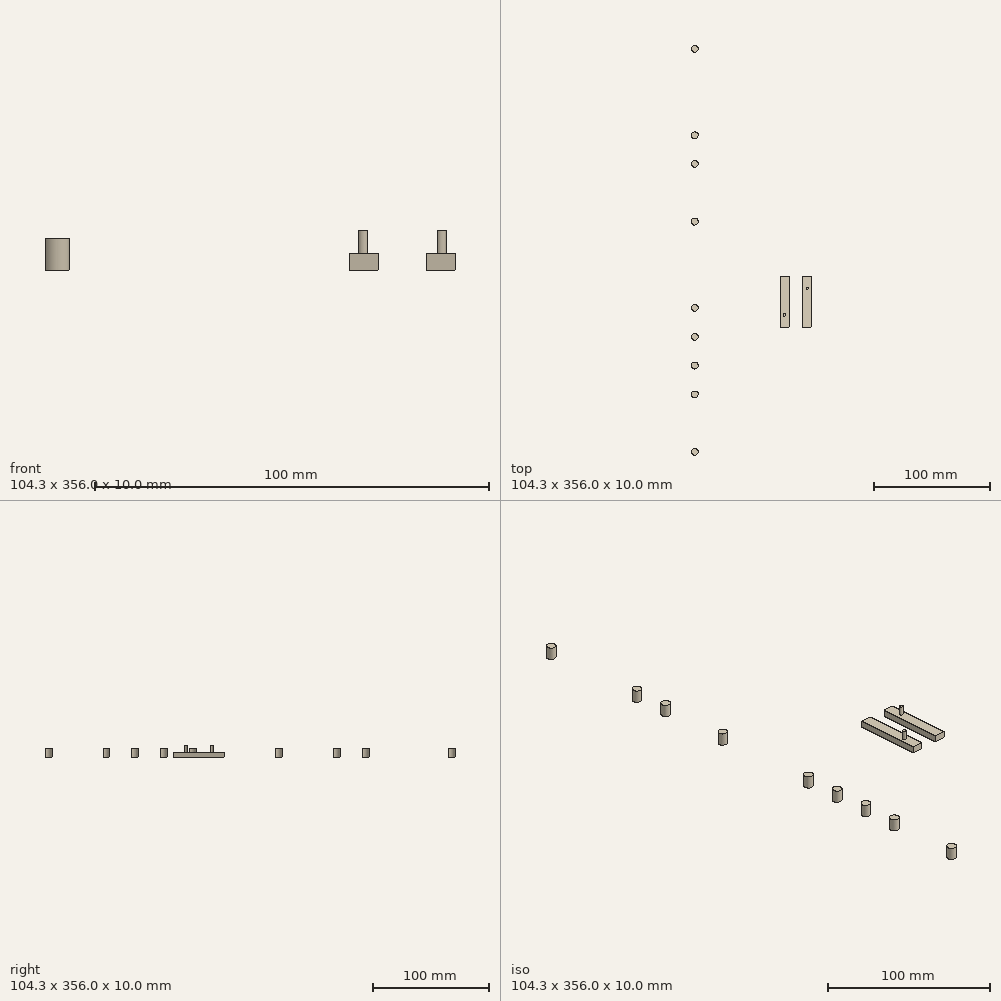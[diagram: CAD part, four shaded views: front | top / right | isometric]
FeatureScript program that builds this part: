
annotation { "Feature Type Name" : "Feature", "Feature Type Description" : "" }
export const myFeature = defineFeature(function(context is Context, id is Id, definition is map)
    precondition{}
    {
        {
            var Q0;
            Q0=qCreatedBy(makeId("Top.planeOp"),FACE);
            var sketch = newSketch(context, id + "F0", { "sketchPlane" : qUnion([Q0])});
            skLineSegment(sketch, "E0.bottom", {"start": v(-46.21, 327.74) * mm, "end": v(-34.21, 327.74) * mm});
            skLineSegment(sketch, "E0.top", {"start": v(-46.21, -72.26) * mm, "end": v(-34.21, -72.26) * mm});
            skLineSegment(sketch, "E0.left", {"start": v(-46.21, 327.74) * mm, "end": v(-46.21, -72.26) * mm});
            skLineSegment(sketch, "E0.right", {"start": v(-34.21, 327.74) * mm, "end": v(-34.21, -72.26) * mm});
            skSolve(sketch);
        }
        {
            var Q0;
            Q0=makeQuery(id+"F0.imprint","IMPRINT",FACE,{"disambiguationData":[TD([[makeQuery(id+"F0.imprint","IMPRINT",EDGE,{"derivedFrom":sQuery(id+"F0.wireOp",EDGE,"E0.bottom")}),-1.0]])]});
            extrude(context, id + "F1", {"entities" : qUnion([Q0]), "depth" : 5 * mm});
        }
        {
            var Q0;
            Q0=makeQuery(id+"F1.opExtrude","CAP_FACE",FACE,{"disambiguationData":[OSD([sQuery(id+"F0.wireOp",EDGE,"E0.bottom"),sQuery(id+"F0.wireOp",EDGE,"E0.top"),sQuery(id+"F0.wireOp",EDGE,"E0.left"),sQuery(id+"F0.wireOp",EDGE,"E0.right")])],"isStart":false});
            var sketch = newSketch(context, id + "F2", { "sketchPlane" : qUnion([Q0])});
            skLineSegment(sketch, "E1", {"start": v(-40.21, 327.74) * mm, "end": v(-40.21, -72.26) * mm});
            skPoint(sketch, "E2", {"position": v(-44.21, 327.74) * mm});
            skLineSegment(sketch, "E3.bottom", {"start": v(-44.21, 327.74) * mm, "end": v(-36.21, 327.74) * mm});
            skLineSegment(sketch, "E3.top", {"start": v(-44.21, -72.26) * mm, "end": v(-36.21, -72.26) * mm});
            skLineSegment(sketch, "E3.left", {"start": v(-44.21, 327.74) * mm, "end": v(-44.21, -72.26) * mm});
            skLineSegment(sketch, "E3.right", {"start": v(-36.21, 327.74) * mm, "end": v(-36.21, -72.26) * mm});
            skSolve(sketch);
        }
        {
            var Q0;
            {var subQ0=sQuery(id+"F2.wireOp",EDGE,"E1");Q0=makeQuery(id+"F2.imprint","IMPRINT",FACE,{"disambiguationData":[TD([[makeQuery(id+"F2.imprint","IMPRINT",EDGE,{"derivedFrom":subQ0}),-1.0]])]});}
            var Q1;
            {var subQ0=sQuery(id+"F2.wireOp",EDGE,"E1");Q1=makeQuery(id+"F2.imprint","IMPRINT",FACE,{"disambiguationData":[TD([[makeQuery(id+"F2.imprint","IMPRINT",EDGE,{"derivedFrom":subQ0}),1.0]])]});}
            extrude(context, id + "F3", {"entities" : qUnion([Q0, Q1]), "operationType" : NewBodyOperationType.ADD, "depth" : 1 * mm});
        }
        {
            var Q0;
            Q0=makeQuery(id+"F3.opExtrude","CAP_FACE",FACE,{"disambiguationData":[OSD([sQuery(id+"F2.wireOp",EDGE,"E3.bottom"),sQuery(id+"F2.wireOp",EDGE,"E3.top"),sQuery(id+"F2.wireOp",EDGE,"E3.left"),sQuery(id+"F2.wireOp",EDGE,"E3.right")])],"isStart":false});
            var sketch = newSketch(context, id + "F4", { "sketchPlane" : qUnion([Q0])});
            skLineSegment(sketch, "E4.0.0", {"start": v(-44.21, -72.26) * mm, "end": v(-44.21, 327.74) * mm});
            skLineSegment(sketch, "E4.0.1", {"start": v(-44.21, 327.74) * mm, "end": v(-46.21, 327.74) * mm});
            skLineSegment(sketch, "E4.0.2", {"start": v(-46.21, 327.74) * mm, "end": v(-46.21, -72.26) * mm});
            skLineSegment(sketch, "E4.0.3", {"start": v(-46.21, -72.26) * mm, "end": v(-44.21, -72.26) * mm});
            skLineSegment(sketch, "E5.0.0", {"start": v(-34.21, 327.74) * mm, "end": v(-36.21, 327.74) * mm});
            skLineSegment(sketch, "E5.0.1", {"start": v(-36.21, 327.74) * mm, "end": v(-36.21, -72.26) * mm});
            skLineSegment(sketch, "E5.0.2", {"start": v(-36.21, -72.26) * mm, "end": v(-34.21, -72.26) * mm});
            skLineSegment(sketch, "E5.0.3", {"start": v(-34.21, -72.26) * mm, "end": v(-34.21, 327.74) * mm});
            skLineSegment(sketch, "E6.bottom", {"start": v(-46.21, -72.26) * mm, "end": v(-34.21, -72.26) * mm});
            skLineSegment(sketch, "E6.top", {"start": v(-46.21, 327.74) * mm, "end": v(-34.21, 327.74) * mm});
            skLineSegment(sketch, "E6.left", {"start": v(-46.21, -72.26) * mm, "end": v(-46.21, 327.74) * mm});
            skSolve(sketch);
        }
        {
            var Q0;
            {var subQ0=sQuery(id+"F4.wireOp",EDGE,"E5.0.1");Q0=makeQuery(id+"F4.imprint","IMPRINT",FACE,{"disambiguationData":[TD([[makeQuery(id+"F4.imprint","IMPRINT",EDGE,{"derivedFrom":subQ0}),1.0]])]});}
            var Q1;
            {var subQ0=sQuery(id+"F4.wireOp",EDGE,"E4.0.0");Q1=makeQuery(id+"F4.imprint","IMPRINT",FACE,{"disambiguationData":[TD([[makeQuery(id+"F4.imprint","IMPRINT",EDGE,{"derivedFrom":subQ0}),1.0]])]});}
            var Q2;
            {var subQ0=sQuery(id+"F4.wireOp",EDGE,"E4.0.0");Q2=makeQuery(id+"F4.imprint","IMPRINT",FACE,{"disambiguationData":[TD([[makeQuery(id+"F4.imprint","IMPRINT",EDGE,{"derivedFrom":subQ0}),-1.0]])]});}
            extrude(context, id + "F5", {"entities" : qUnion([Q0, Q1, Q2]), "operationType" : NewBodyOperationType.ADD, "depth" : 2 * mm});
        }
        {
            var Q0;
            Q0=makeQuery(id+"F5.opExtrude","CAP_FACE",FACE,{"disambiguationData":[OSD([sQuery(id+"F4.wireOp",EDGE,"E6.bottom"),sQuery(id+"F4.wireOp",EDGE,"E6.top"),sQuery(id+"F4.wireOp",EDGE,"E6.left"),sQuery(id+"F4.wireOp",EDGE,"E5.0.3")])],"isStart":false});
            var sketch = newSketch(context, id + "F6", { "sketchPlane" : qUnion([Q0])});
            skLineSegment(sketch, "E7", {"start": v(-40.21, -72.26) * mm, "end": v(-40.21, 327.74) * mm});
            skCircle(sketch, "E8", {"center": v(-40.21, -60.26) * mm, "radius": 3 * mm});
            skCircle(sketch, "E9", {"center": v(-40.21, -35.26) * mm, "radius": 3 * mm});
            skCircle(sketch, "E10.0.1.0", {"center": v(-40.21, -10.26) * mm, "radius": 3 * mm});
            skCircle(sketch, "E10.0.1.1", {"center": v(-40.21, 14.74) * mm, "radius": 3 * mm});
            skCircle(sketch, "E10.0.2.0", {"center": v(-40.21, 39.74) * mm, "radius": 3 * mm});
            skCircle(sketch, "E10.0.2.1", {"center": v(-40.21, 64.74) * mm, "radius": 3 * mm});
            skCircle(sketch, "E10.0.3.0", {"center": v(-40.21, 89.74) * mm, "radius": 3 * mm});
            skCircle(sketch, "E10.0.3.1", {"center": v(-40.21, 114.74) * mm, "radius": 3 * mm});
            skCircle(sketch, "E10.0.4.0", {"center": v(-40.21, 139.74) * mm, "radius": 3 * mm});
            skCircle(sketch, "E10.0.4.1", {"center": v(-40.21, 164.74) * mm, "radius": 3 * mm});
            skCircle(sketch, "E10.0.5.0", {"center": v(-40.21, 189.74) * mm, "radius": 3 * mm});
            skCircle(sketch, "E10.0.5.1", {"center": v(-40.21, 214.74) * mm, "radius": 3 * mm});
            skCircle(sketch, "E10.0.6.0", {"center": v(-40.21, 239.74) * mm, "radius": 3 * mm});
            skCircle(sketch, "E10.0.6.1", {"center": v(-40.21, 264.74) * mm, "radius": 3 * mm});
            skCircle(sketch, "E10.0.7.0", {"center": v(-40.21, 289.74) * mm, "radius": 3 * mm});
            skCircle(sketch, "E10.0.7.1", {"center": v(-40.21, 314.74) * mm, "radius": 3 * mm});
            skLineSegment(sketch, "E10.direction1", {"start": v(-40.21, -60.26) * mm, "end": v(-40.31, -60.26) * mm, "construction": true});
            skLineSegment(sketch, "E10.direction2", {"start": v(-40.21, -60.26) * mm, "end": v(-40.21, -10.26) * mm, "construction": true});
            skSolve(sketch);
        }
        {
            var Q0;
            {var subQ0=sQuery(id+"F6.wireOp",EDGE,"E8");var subQ1=sQuery(id+"F6.wireOp",EDGE,"E7");var subQ2=makeQuery(id+"F6.imprint","INTERSECT",VERTEX,{"disambiguationData":[OD(0.0)],"derivedFrom":[subQ1,subQ0]});Q0=makeQuery(id+"F6.imprint","IMPRINT",FACE,{"disambiguationData":[TD([[makeQuery(id+"F6.imprint","IMPRINT",EDGE,{"disambiguationData":[TD([[subQ2,-1.0]])],"derivedFrom":subQ1}),-1.0]])]});}
            var Q1;
            {var subQ0=sQuery(id+"F6.wireOp",EDGE,"E9");var subQ1=sQuery(id+"F6.wireOp",EDGE,"E7");var subQ2=makeQuery(id+"F6.imprint","INTERSECT",VERTEX,{"disambiguationData":[OD(0.0)],"derivedFrom":[subQ1,subQ0]});Q1=makeQuery(id+"F6.imprint","IMPRINT",FACE,{"disambiguationData":[TD([[makeQuery(id+"F6.imprint","IMPRINT",EDGE,{"disambiguationData":[TD([[subQ2,-1.0]])],"derivedFrom":subQ1}),-1.0]])]});}
            var Q2;
            {var subQ0=sQuery(id+"F6.wireOp",EDGE,"E9");var subQ1=sQuery(id+"F6.wireOp",EDGE,"E7");var subQ2=makeQuery(id+"F6.imprint","INTERSECT",VERTEX,{"disambiguationData":[OD(0.0)],"derivedFrom":[subQ1,subQ0]});Q2=makeQuery(id+"F6.imprint","IMPRINT",FACE,{"disambiguationData":[TD([[makeQuery(id+"F6.imprint","IMPRINT",EDGE,{"disambiguationData":[TD([[subQ2,-1.0]])],"derivedFrom":subQ1}),1.0]])]});}
            var Q3;
            {var subQ0=sQuery(id+"F6.wireOp",EDGE,"E8");var subQ1=sQuery(id+"F6.wireOp",EDGE,"E7");var subQ2=makeQuery(id+"F6.imprint","INTERSECT",VERTEX,{"disambiguationData":[OD(0.0)],"derivedFrom":[subQ1,subQ0]});Q3=makeQuery(id+"F6.imprint","IMPRINT",FACE,{"disambiguationData":[TD([[makeQuery(id+"F6.imprint","IMPRINT",EDGE,{"disambiguationData":[TD([[subQ2,-1.0]])],"derivedFrom":subQ1}),1.0]])]});}
            var Q4;
            {var subQ0=sQuery(id+"F6.wireOp",EDGE,"E10.0.1.0");var subQ1=sQuery(id+"F6.wireOp",EDGE,"E7");var subQ2=makeQuery(id+"F6.imprint","INTERSECT",VERTEX,{"disambiguationData":[OD(0.0)],"derivedFrom":[subQ1,subQ0]});Q4=makeQuery(id+"F6.imprint","IMPRINT",FACE,{"disambiguationData":[TD([[makeQuery(id+"F6.imprint","IMPRINT",EDGE,{"disambiguationData":[TD([[subQ2,-1.0]])],"derivedFrom":subQ1}),-1.0]])]});}
            var Q5;
            {var subQ0=sQuery(id+"F6.wireOp",EDGE,"E10.0.1.0");var subQ1=sQuery(id+"F6.wireOp",EDGE,"E7");var subQ2=makeQuery(id+"F6.imprint","INTERSECT",VERTEX,{"disambiguationData":[OD(0.0)],"derivedFrom":[subQ1,subQ0]});Q5=makeQuery(id+"F6.imprint","IMPRINT",FACE,{"disambiguationData":[TD([[makeQuery(id+"F6.imprint","IMPRINT",EDGE,{"disambiguationData":[TD([[subQ2,-1.0]])],"derivedFrom":subQ1}),1.0]])]});}
            var Q6;
            {var subQ0=sQuery(id+"F6.wireOp",EDGE,"E10.0.1.1");var subQ1=sQuery(id+"F6.wireOp",EDGE,"E7");var subQ2=makeQuery(id+"F6.imprint","INTERSECT",VERTEX,{"disambiguationData":[OD(0.0)],"derivedFrom":[subQ1,subQ0]});Q6=makeQuery(id+"F6.imprint","IMPRINT",FACE,{"disambiguationData":[TD([[makeQuery(id+"F6.imprint","IMPRINT",EDGE,{"disambiguationData":[TD([[subQ2,-1.0]])],"derivedFrom":subQ1}),-1.0]])]});}
            var Q7;
            {var subQ0=sQuery(id+"F6.wireOp",EDGE,"E10.0.1.1");var subQ1=sQuery(id+"F6.wireOp",EDGE,"E7");var subQ2=makeQuery(id+"F6.imprint","INTERSECT",VERTEX,{"disambiguationData":[OD(0.0)],"derivedFrom":[subQ1,subQ0]});Q7=makeQuery(id+"F6.imprint","IMPRINT",FACE,{"disambiguationData":[TD([[makeQuery(id+"F6.imprint","IMPRINT",EDGE,{"disambiguationData":[TD([[subQ2,-1.0]])],"derivedFrom":subQ1}),1.0]])]});}
            var Q8;
            {var subQ0=sQuery(id+"F6.wireOp",EDGE,"E10.0.2.0");var subQ1=sQuery(id+"F6.wireOp",EDGE,"E7");var subQ2=makeQuery(id+"F6.imprint","INTERSECT",VERTEX,{"disambiguationData":[OD(0.0)],"derivedFrom":[subQ1,subQ0]});Q8=makeQuery(id+"F6.imprint","IMPRINT",FACE,{"disambiguationData":[TD([[makeQuery(id+"F6.imprint","IMPRINT",EDGE,{"disambiguationData":[TD([[subQ2,-1.0]])],"derivedFrom":subQ1}),-1.0]])]});}
            var Q9;
            {var subQ0=sQuery(id+"F6.wireOp",EDGE,"E10.0.2.0");var subQ1=sQuery(id+"F6.wireOp",EDGE,"E7");var subQ2=makeQuery(id+"F6.imprint","INTERSECT",VERTEX,{"disambiguationData":[OD(0.0)],"derivedFrom":[subQ1,subQ0]});Q9=makeQuery(id+"F6.imprint","IMPRINT",FACE,{"disambiguationData":[TD([[makeQuery(id+"F6.imprint","IMPRINT",EDGE,{"disambiguationData":[TD([[subQ2,-1.0]])],"derivedFrom":subQ1}),1.0]])]});}
            var Q10;
            {var subQ0=sQuery(id+"F6.wireOp",EDGE,"E10.0.2.1");var subQ1=sQuery(id+"F6.wireOp",EDGE,"E7");var subQ2=makeQuery(id+"F6.imprint","INTERSECT",VERTEX,{"disambiguationData":[OD(0.0)],"derivedFrom":[subQ1,subQ0]});Q10=makeQuery(id+"F6.imprint","IMPRINT",FACE,{"disambiguationData":[TD([[makeQuery(id+"F6.imprint","IMPRINT",EDGE,{"disambiguationData":[TD([[subQ2,-1.0]])],"derivedFrom":subQ1}),-1.0]])]});}
            var Q11;
            {var subQ0=sQuery(id+"F6.wireOp",EDGE,"E10.0.2.1");var subQ1=sQuery(id+"F6.wireOp",EDGE,"E7");var subQ2=makeQuery(id+"F6.imprint","INTERSECT",VERTEX,{"disambiguationData":[OD(0.0)],"derivedFrom":[subQ1,subQ0]});Q11=makeQuery(id+"F6.imprint","IMPRINT",FACE,{"disambiguationData":[TD([[makeQuery(id+"F6.imprint","IMPRINT",EDGE,{"disambiguationData":[TD([[subQ2,-1.0]])],"derivedFrom":subQ1}),1.0]])]});}
            var Q12;
            {var subQ0=sQuery(id+"F6.wireOp",EDGE,"E10.0.3.0");var subQ1=sQuery(id+"F6.wireOp",EDGE,"E7");var subQ2=makeQuery(id+"F6.imprint","INTERSECT",VERTEX,{"disambiguationData":[OD(0.0)],"derivedFrom":[subQ1,subQ0]});Q12=makeQuery(id+"F6.imprint","IMPRINT",FACE,{"disambiguationData":[TD([[makeQuery(id+"F6.imprint","IMPRINT",EDGE,{"disambiguationData":[TD([[subQ2,-1.0]])],"derivedFrom":subQ1}),-1.0]])]});}
            var Q13;
            {var subQ0=sQuery(id+"F6.wireOp",EDGE,"E10.0.3.0");var subQ1=sQuery(id+"F6.wireOp",EDGE,"E7");var subQ2=makeQuery(id+"F6.imprint","INTERSECT",VERTEX,{"disambiguationData":[OD(0.0)],"derivedFrom":[subQ1,subQ0]});Q13=makeQuery(id+"F6.imprint","IMPRINT",FACE,{"disambiguationData":[TD([[makeQuery(id+"F6.imprint","IMPRINT",EDGE,{"disambiguationData":[TD([[subQ2,-1.0]])],"derivedFrom":subQ1}),1.0]])]});}
            var Q14;
            {var subQ0=sQuery(id+"F6.wireOp",EDGE,"E10.0.3.1");var subQ1=sQuery(id+"F6.wireOp",EDGE,"E7");var subQ2=makeQuery(id+"F6.imprint","INTERSECT",VERTEX,{"disambiguationData":[OD(0.0)],"derivedFrom":[subQ1,subQ0]});Q14=makeQuery(id+"F6.imprint","IMPRINT",FACE,{"disambiguationData":[TD([[makeQuery(id+"F6.imprint","IMPRINT",EDGE,{"disambiguationData":[TD([[subQ2,-1.0]])],"derivedFrom":subQ1}),-1.0]])]});}
            var Q15;
            {var subQ0=sQuery(id+"F6.wireOp",EDGE,"E10.0.3.1");var subQ1=sQuery(id+"F6.wireOp",EDGE,"E7");var subQ2=makeQuery(id+"F6.imprint","INTERSECT",VERTEX,{"disambiguationData":[OD(0.0)],"derivedFrom":[subQ1,subQ0]});Q15=makeQuery(id+"F6.imprint","IMPRINT",FACE,{"disambiguationData":[TD([[makeQuery(id+"F6.imprint","IMPRINT",EDGE,{"disambiguationData":[TD([[subQ2,-1.0]])],"derivedFrom":subQ1}),1.0]])]});}
            var Q16;
            {var subQ0=sQuery(id+"F6.wireOp",EDGE,"E10.0.4.0");var subQ1=sQuery(id+"F6.wireOp",EDGE,"E7");var subQ2=makeQuery(id+"F6.imprint","INTERSECT",VERTEX,{"disambiguationData":[OD(0.0)],"derivedFrom":[subQ1,subQ0]});Q16=makeQuery(id+"F6.imprint","IMPRINT",FACE,{"disambiguationData":[TD([[makeQuery(id+"F6.imprint","IMPRINT",EDGE,{"disambiguationData":[TD([[subQ2,-1.0]])],"derivedFrom":subQ1}),-1.0]])]});}
            var Q17;
            {var subQ0=sQuery(id+"F6.wireOp",EDGE,"E10.0.4.0");var subQ1=sQuery(id+"F6.wireOp",EDGE,"E7");var subQ2=makeQuery(id+"F6.imprint","INTERSECT",VERTEX,{"disambiguationData":[OD(0.0)],"derivedFrom":[subQ1,subQ0]});Q17=makeQuery(id+"F6.imprint","IMPRINT",FACE,{"disambiguationData":[TD([[makeQuery(id+"F6.imprint","IMPRINT",EDGE,{"disambiguationData":[TD([[subQ2,-1.0]])],"derivedFrom":subQ1}),1.0]])]});}
            var Q18;
            {var subQ0=sQuery(id+"F6.wireOp",EDGE,"E10.0.4.1");var subQ1=sQuery(id+"F6.wireOp",EDGE,"E7");var subQ2=makeQuery(id+"F6.imprint","INTERSECT",VERTEX,{"disambiguationData":[OD(0.0)],"derivedFrom":[subQ1,subQ0]});Q18=makeQuery(id+"F6.imprint","IMPRINT",FACE,{"disambiguationData":[TD([[makeQuery(id+"F6.imprint","IMPRINT",EDGE,{"disambiguationData":[TD([[subQ2,-1.0]])],"derivedFrom":subQ1}),-1.0]])]});}
            var Q19;
            {var subQ0=sQuery(id+"F6.wireOp",EDGE,"E10.0.4.1");var subQ1=sQuery(id+"F6.wireOp",EDGE,"E7");var subQ2=makeQuery(id+"F6.imprint","INTERSECT",VERTEX,{"disambiguationData":[OD(0.0)],"derivedFrom":[subQ1,subQ0]});Q19=makeQuery(id+"F6.imprint","IMPRINT",FACE,{"disambiguationData":[TD([[makeQuery(id+"F6.imprint","IMPRINT",EDGE,{"disambiguationData":[TD([[subQ2,-1.0]])],"derivedFrom":subQ1}),1.0]])]});}
            var Q20;
            {var subQ0=sQuery(id+"F6.wireOp",EDGE,"E10.0.5.0");var subQ1=sQuery(id+"F6.wireOp",EDGE,"E7");var subQ2=makeQuery(id+"F6.imprint","INTERSECT",VERTEX,{"disambiguationData":[OD(0.0)],"derivedFrom":[subQ1,subQ0]});Q20=makeQuery(id+"F6.imprint","IMPRINT",FACE,{"disambiguationData":[TD([[makeQuery(id+"F6.imprint","IMPRINT",EDGE,{"disambiguationData":[TD([[subQ2,-1.0]])],"derivedFrom":subQ1}),-1.0]])]});}
            var Q21;
            {var subQ0=sQuery(id+"F6.wireOp",EDGE,"E10.0.5.0");var subQ1=sQuery(id+"F6.wireOp",EDGE,"E7");var subQ2=makeQuery(id+"F6.imprint","INTERSECT",VERTEX,{"disambiguationData":[OD(0.0)],"derivedFrom":[subQ1,subQ0]});Q21=makeQuery(id+"F6.imprint","IMPRINT",FACE,{"disambiguationData":[TD([[makeQuery(id+"F6.imprint","IMPRINT",EDGE,{"disambiguationData":[TD([[subQ2,-1.0]])],"derivedFrom":subQ1}),1.0]])]});}
            var Q22;
            {var subQ0=sQuery(id+"F6.wireOp",EDGE,"E10.0.5.1");var subQ1=sQuery(id+"F6.wireOp",EDGE,"E7");var subQ2=makeQuery(id+"F6.imprint","INTERSECT",VERTEX,{"disambiguationData":[OD(0.0)],"derivedFrom":[subQ1,subQ0]});Q22=makeQuery(id+"F6.imprint","IMPRINT",FACE,{"disambiguationData":[TD([[makeQuery(id+"F6.imprint","IMPRINT",EDGE,{"disambiguationData":[TD([[subQ2,-1.0]])],"derivedFrom":subQ1}),-1.0]])]});}
            var Q23;
            {var subQ0=sQuery(id+"F6.wireOp",EDGE,"E10.0.5.1");var subQ1=sQuery(id+"F6.wireOp",EDGE,"E7");var subQ2=makeQuery(id+"F6.imprint","INTERSECT",VERTEX,{"disambiguationData":[OD(0.0)],"derivedFrom":[subQ1,subQ0]});Q23=makeQuery(id+"F6.imprint","IMPRINT",FACE,{"disambiguationData":[TD([[makeQuery(id+"F6.imprint","IMPRINT",EDGE,{"disambiguationData":[TD([[subQ2,-1.0]])],"derivedFrom":subQ1}),1.0]])]});}
            var Q24;
            {var subQ0=sQuery(id+"F6.wireOp",EDGE,"E10.0.6.0");var subQ1=sQuery(id+"F6.wireOp",EDGE,"E7");var subQ2=makeQuery(id+"F6.imprint","INTERSECT",VERTEX,{"disambiguationData":[OD(0.0)],"derivedFrom":[subQ1,subQ0]});Q24=makeQuery(id+"F6.imprint","IMPRINT",FACE,{"disambiguationData":[TD([[makeQuery(id+"F6.imprint","IMPRINT",EDGE,{"disambiguationData":[TD([[subQ2,-1.0]])],"derivedFrom":subQ1}),-1.0]])]});}
            var Q25;
            {var subQ0=sQuery(id+"F6.wireOp",EDGE,"E10.0.6.0");var subQ1=sQuery(id+"F6.wireOp",EDGE,"E7");var subQ2=makeQuery(id+"F6.imprint","INTERSECT",VERTEX,{"disambiguationData":[OD(0.0)],"derivedFrom":[subQ1,subQ0]});Q25=makeQuery(id+"F6.imprint","IMPRINT",FACE,{"disambiguationData":[TD([[makeQuery(id+"F6.imprint","IMPRINT",EDGE,{"disambiguationData":[TD([[subQ2,-1.0]])],"derivedFrom":subQ1}),1.0]])]});}
            var Q26;
            {var subQ0=sQuery(id+"F6.wireOp",EDGE,"E10.0.6.1");var subQ1=sQuery(id+"F6.wireOp",EDGE,"E7");var subQ2=makeQuery(id+"F6.imprint","INTERSECT",VERTEX,{"disambiguationData":[OD(0.0)],"derivedFrom":[subQ1,subQ0]});Q26=makeQuery(id+"F6.imprint","IMPRINT",FACE,{"disambiguationData":[TD([[makeQuery(id+"F6.imprint","IMPRINT",EDGE,{"disambiguationData":[TD([[subQ2,-1.0]])],"derivedFrom":subQ1}),-1.0]])]});}
            var Q27;
            {var subQ0=sQuery(id+"F6.wireOp",EDGE,"E10.0.6.1");var subQ1=sQuery(id+"F6.wireOp",EDGE,"E7");var subQ2=makeQuery(id+"F6.imprint","INTERSECT",VERTEX,{"disambiguationData":[OD(0.0)],"derivedFrom":[subQ1,subQ0]});Q27=makeQuery(id+"F6.imprint","IMPRINT",FACE,{"disambiguationData":[TD([[makeQuery(id+"F6.imprint","IMPRINT",EDGE,{"disambiguationData":[TD([[subQ2,-1.0]])],"derivedFrom":subQ1}),1.0]])]});}
            var Q28;
            {var subQ0=sQuery(id+"F6.wireOp",EDGE,"E10.0.7.0");var subQ1=sQuery(id+"F6.wireOp",EDGE,"E7");var subQ2=makeQuery(id+"F6.imprint","INTERSECT",VERTEX,{"disambiguationData":[OD(0.0)],"derivedFrom":[subQ1,subQ0]});Q28=makeQuery(id+"F6.imprint","IMPRINT",FACE,{"disambiguationData":[TD([[makeQuery(id+"F6.imprint","IMPRINT",EDGE,{"disambiguationData":[TD([[subQ2,-1.0]])],"derivedFrom":subQ1}),-1.0]])]});}
            var Q29;
            {var subQ0=sQuery(id+"F6.wireOp",EDGE,"E10.0.7.0");var subQ1=sQuery(id+"F6.wireOp",EDGE,"E7");var subQ2=makeQuery(id+"F6.imprint","INTERSECT",VERTEX,{"disambiguationData":[OD(0.0)],"derivedFrom":[subQ1,subQ0]});Q29=makeQuery(id+"F6.imprint","IMPRINT",FACE,{"disambiguationData":[TD([[makeQuery(id+"F6.imprint","IMPRINT",EDGE,{"disambiguationData":[TD([[subQ2,-1.0]])],"derivedFrom":subQ1}),1.0]])]});}
            var Q30;
            {var subQ0=sQuery(id+"F6.wireOp",EDGE,"E10.0.7.1");var subQ1=sQuery(id+"F6.wireOp",EDGE,"E7");var subQ2=makeQuery(id+"F6.imprint","INTERSECT",VERTEX,{"disambiguationData":[OD(0.0)],"derivedFrom":[subQ1,subQ0]});Q30=makeQuery(id+"F6.imprint","IMPRINT",FACE,{"disambiguationData":[TD([[makeQuery(id+"F6.imprint","IMPRINT",EDGE,{"disambiguationData":[TD([[subQ2,-1.0]])],"derivedFrom":subQ1}),-1.0]])]});}
            var Q31;
            {var subQ0=sQuery(id+"F6.wireOp",EDGE,"E10.0.7.1");var subQ1=sQuery(id+"F6.wireOp",EDGE,"E7");var subQ2=makeQuery(id+"F6.imprint","INTERSECT",VERTEX,{"disambiguationData":[OD(0.0)],"derivedFrom":[subQ1,subQ0]});Q31=makeQuery(id+"F6.imprint","IMPRINT",FACE,{"disambiguationData":[TD([[makeQuery(id+"F6.imprint","IMPRINT",EDGE,{"disambiguationData":[TD([[subQ2,-1.0]])],"derivedFrom":subQ1}),1.0]])]});}
            extrude(context, id + "F7", {"entities" : qUnion([Q0, Q1, Q2, Q3, Q4, Q5, Q6, Q7, Q8, Q9, Q10, Q11, Q12, Q13, Q14, Q15, Q16, Q17, Q18, Q19, Q20, Q21, Q22, Q23, Q24, Q25, Q26, Q27, Q28, Q29, Q30, Q31]), "operationType" : NewBodyOperationType.REMOVE, "oppositeDirection" : true, "depth" : 25 * mm});
        }
        {
            var Q0;
            Q0=qCreatedBy(makeId("Top.planeOp"),FACE);
            var sketch = newSketch(context, id + "F8", { "sketchPlane" : qUnion([Q0])});
            skLineSegment(sketch, "E11.bottom", {"start": v(34.06, 92.56) * mm, "end": v(61.06, 92.56) * mm});
            skLineSegment(sketch, "E11.top", {"start": v(34.06, 47.56) * mm, "end": v(61.06, 47.56) * mm});
            skLineSegment(sketch, "E11.left", {"start": v(34.06, 92.56) * mm, "end": v(34.06, 47.56) * mm});
            skLineSegment(sketch, "E11.right", {"start": v(61.06, 92.56) * mm, "end": v(61.06, 47.56) * mm});
            skSolve(sketch);
        }
        {
            var Q0;
            Q0=makeQuery(id+"F8.imprint","IMPRINT",FACE,{"disambiguationData":[TD([[makeQuery(id+"F8.imprint","IMPRINT",EDGE,{"derivedFrom":sQuery(id+"F8.wireOp",EDGE,"E11.bottom")}),-1.0]])]});
            extrude(context, id + "F9", {"entities" : qUnion([Q0]), "depth" : 10 * mm});
        }
        {
            var Q0;
            Q0=makeQuery(id+"F9.opExtrude","CAP_FACE",FACE,{"disambiguationData":[OSD([sQuery(id+"F8.wireOp",EDGE,"E11.bottom"),sQuery(id+"F8.wireOp",EDGE,"E11.top"),sQuery(id+"F8.wireOp",EDGE,"E11.left"),sQuery(id+"F8.wireOp",EDGE,"E11.right")])],"isStart":true});
            var sketch = newSketch(context, id + "F10", { "sketchPlane" : qUnion([Q0])});
            skLineSegment(sketch, "E12", {"start": v(47.56, -47.56) * mm, "end": v(47.56, -92.56) * mm});
            skLineSegment(sketch, "E13.bottom", {"start": v(53.56, -47.56) * mm, "end": v(41.56, -47.56) * mm});
            skLineSegment(sketch, "E13.top", {"start": v(53.56, -92.56) * mm, "end": v(41.56, -92.56) * mm});
            skLineSegment(sketch, "E13.left", {"start": v(53.56, -47.56) * mm, "end": v(53.56, -92.56) * mm});
            skLineSegment(sketch, "E13.right", {"start": v(41.56, -47.56) * mm, "end": v(41.56, -92.56) * mm});
            skSolve(sketch);
        }
        {
            var Q0;
            {var subQ0=sQuery(id+"F10.wireOp",EDGE,"E12");Q0=makeQuery(id+"F10.imprint","IMPRINT",FACE,{"disambiguationData":[TD([[makeQuery(id+"F10.imprint","IMPRINT",EDGE,{"derivedFrom":subQ0}),1.0]])]});}
            var Q1;
            {var subQ0=sQuery(id+"F10.wireOp",EDGE,"E12");Q1=makeQuery(id+"F10.imprint","IMPRINT",FACE,{"disambiguationData":[TD([[makeQuery(id+"F10.imprint","IMPRINT",EDGE,{"derivedFrom":subQ0}),-1.0]])]});}
            extrude(context, id + "F11", {"entities" : qUnion([Q0, Q1]), "operationType" : NewBodyOperationType.REMOVE, "oppositeDirection" : true, "depth" : (10 - 4) * mm});
        }
        {
            var Q0;
            Q0=makeQuery(id+"F9.opExtrude","CAP_FACE",FACE,{"disambiguationData":[OSD([sQuery(id+"F8.wireOp",EDGE,"E11.bottom"),sQuery(id+"F8.wireOp",EDGE,"E11.top"),sQuery(id+"F8.wireOp",EDGE,"E11.left"),sQuery(id+"F8.wireOp",EDGE,"E11.right")])],"isStart":false});
            var sketch = newSketch(context, id + "F12", { "sketchPlane" : qUnion([Q0])});
            skCircle(sketch, "E14", {"center": v(37.6, 81.56) * mm, "radius": 1.15 * mm});
            skCircle(sketch, "E15.MirrorC", {"center": v(57.5, 81.56) * mm, "radius": 1.15 * mm});
            skCircle(sketch, "E16.MirrorC", {"center": v(37.6, 58.56) * mm, "radius": 1.15 * mm});
            skCircle(sketch, "E17.MirrorC", {"center": v(57.5, 58.56) * mm, "radius": 1.15 * mm});
            skSolve(sketch);
        }
        {
            var Q0;
            Q0=makeQuery(id+"F12.imprint","IMPRINT",FACE,{"disambiguationData":[TD([[makeQuery(id+"F12.imprint","IMPRINT",EDGE,{"derivedFrom":sQuery(id+"F12.wireOp",EDGE,"E14")}),1.0]])]});
            var Q1;
            Q1=makeQuery(id+"F12.imprint","IMPRINT",FACE,{"disambiguationData":[TD([[makeQuery(id+"F12.imprint","IMPRINT",EDGE,{"derivedFrom":sQuery(id+"F12.wireOp",EDGE,"E15.MirrorC")}),-1.0]])]});
            var Q2;
            Q2=makeQuery(id+"F12.imprint","IMPRINT",FACE,{"disambiguationData":[TD([[makeQuery(id+"F12.imprint","IMPRINT",EDGE,{"derivedFrom":sQuery(id+"F12.wireOp",EDGE,"E16.MirrorC")}),-1.0]])]});
            var Q3;
            Q3=makeQuery(id+"F12.imprint","IMPRINT",FACE,{"disambiguationData":[TD([[makeQuery(id+"F12.imprint","IMPRINT",EDGE,{"derivedFrom":sQuery(id+"F12.wireOp",EDGE,"E17.MirrorC")}),1.0]])]});
            extrude(context, id + "F13", {"entities" : qUnion([Q0, Q1, Q2, Q3]), "operationType" : NewBodyOperationType.REMOVE, "oppositeDirection" : true, "depth" : 5.7 * mm});
        }
    });
